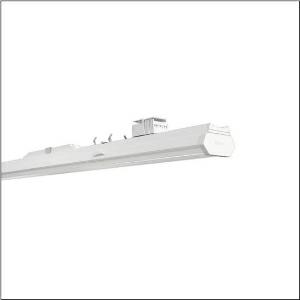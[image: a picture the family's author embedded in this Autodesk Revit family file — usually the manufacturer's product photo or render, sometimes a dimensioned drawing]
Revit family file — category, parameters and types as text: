
# Revit family: licross_r__11_protected_ho_51tp11mn4gxs_ec8e
name_source: partatom
category: Lighting Fixtures
units: mm (PartAtom-declared; Revit-internal decimal feet)

## family parameters
Cut with Voids When Loaded = No
Host = Face
Light Source = No
Part Type = Normal
Room Calculation Point = No
Round Connector Dimension = Use Diameter
Shared = No

## types (1)
- --- (1 x LED, 16070 lm, 87.4 W, 4000K)
    Apparent Load = 87 VA
    CIE Flux Codes = 84 94 98 99 100
    Color Rendering = 80
    Color Temperature = 4000K
    Default Elevation = 1800 mm
    Description = Licross® 11 Protected HO, luminaire insert, of sheet steel, galvanised, coil coated, white, length: 1.500mm, width: 90mm, height: 101mm, LED rated luminous flux: 16.070lm, light colour: 840, control gear: ON/OFF Multilumen, with plug, 3-pole, with phase selection, mains connection: 220..240V, AC, 50/60Hz, rated input power: 87W, halogen-free wiring, primary light control with lens, of plastic, primary optical cover: cover, of PMMA, light emission: direct distribution, primary light characteristic: symmetric, protection rating (complete): IP64, insulation class (complete): insulation class I (protective earthing), certification: CE, ENEC, VDE, UKCA, protection symbol: D if used in an environment with conductive dust loads with corresponding accessories, impact resistance: IK06, permissible ambient temperature for indoor applications: -35..+35°C, corresponds to IFS (International Featured Standards) requirements for safety and quality in the food industry, reducing of maximum allowable ambient temperature of 5°C with ceiling mounting, LABS conformity tested according to VDMA 24364:2018-05, packaging unit: 1 piece
    Height = 92 mm
    Lamp = 1 x LED
    Lamp Light Flux = 16070 lm
    Lamp Power = 87.4 W
    Lamp count = 1
    Length = 1500 mm
    Luminous efficacy = 184 lm/W
    Manufacturer = Siteco
    ModVariant = No
    Model = 51TP11MN4GXS
    Mounting Place = Ceiling
    Mounting Type = Pendant
    Number of Poles = 1
    OnlyDefault = Yes
    Power Factor = 1
    Product Name = Licross® 11 Protected HO
    Product group = luminaire insert
    ProductGroupID = 902
    Protection Class = Protection class I
    Protection Degree = IP 64
    RLX_Detail_Level = 1
    RLX_Emergency_Light_Flux = 0 lm
    RLX_Emergency_Type = 0
    RLX_Emergency_Type_DB = No
    RlxData = <blob elided: 21977 chars, md5=edec94e7>
    Socket = socket
    Standby Power = 0 W
    System Light Flux = 16070 lm
    System Power = 87 W
    Type Comments = factory setting: luminous flux: 100 % | (A | C | E) | 203 mA
    Type Image = l_1256148.jpg
    URL = http://relux.com
    VarID = @adj_085840
    Voltage = 0 V
    Weight = 0.00 kg
    Width = 88 mm

## geometry (parser evidence)
native form markers: Blend x4, Sweep x11
no freeform markers — native parametric forms only
